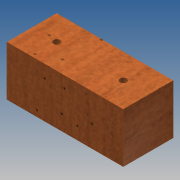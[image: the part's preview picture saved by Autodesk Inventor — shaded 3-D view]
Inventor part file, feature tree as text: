
AUTODESK INVENTOR PART (.ipt)
format: ipt  version: 2014 SP1 (Build 180222100, 222)  size: 109,056 bytes
history: native  units: in
note: dims shown in document units (in); Inventor stores cm internally (conversion verified against a paired STEP export)
features: sketch x2, extrude x1, hole x1
ambient origin geometry x8: Origin, YZ Plane, XZ Plane, XY Plane, X Axis, Y Axis, Z Axis, Center Point
bodies: Solid1 (feature_tree)
feature tree (4):
  extrude  "Extrusion1"  Depth=1.5in
  hole  "Hole1"  [1 undecoded]
  sketch  "Sketch1"  dims[d0=3.5in d1=1.5in]
  sketch  "Sketch2"  dims[d2=1.5in d3=0.0in d4=0.75in d5=0.75in d6=0.7874in d8=2.0in d9=0.3937in d11=1.0in d13=0.201in d14=0.75in d15=0.385in d16=0.25in d17=0.5635in d18=2.0in d19=0.8108in]
note: 1 required parameter value undecoded (feature->parameter linkage not recoverable at this tier; creation-order binding heuristic only, values carry confidence <= 0.55)
